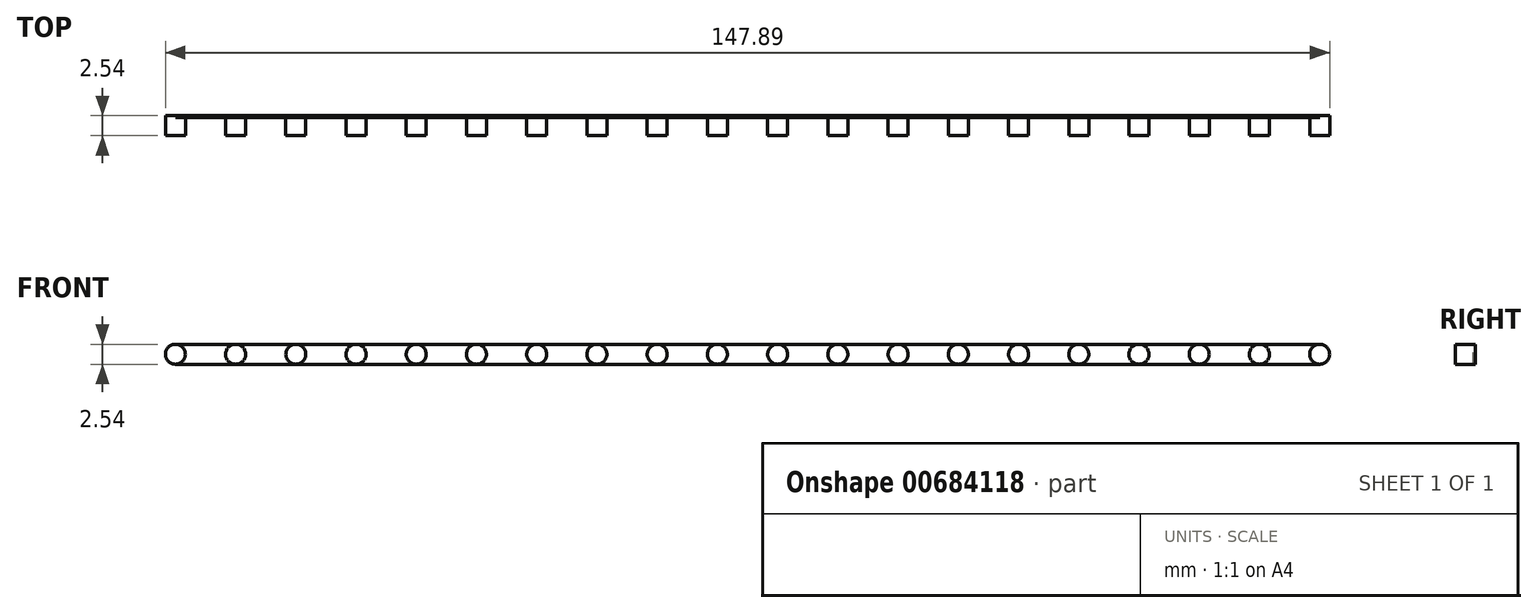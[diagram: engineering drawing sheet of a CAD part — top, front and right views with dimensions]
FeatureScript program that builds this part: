
annotation { "Feature Type Name" : "Feature", "Feature Type Description" : "" }
export const myFeature = defineFeature(function(context is Context, id is Id, definition is map)
    precondition{}
    {
        {
            var Q0;
            Q0=qCreatedBy(makeId("Front.planeOp"),FACE);
            var sketch = newSketch(context, id + "F0", { "sketchPlane" : qUnion([Q0])});
            skCircle(sketch, "E0", {"center": v(0, 0) * mm, "radius": 1.27 * mm});
            skCircle(sketch, "E1.1.0.0", {"center": v(7.65, 0) * mm, "radius": 1.27 * mm});
            skCircle(sketch, "E1.2.0.0", {"center": v(15.3, 0) * mm, "radius": 1.27 * mm});
            skLineSegment(sketch, "E1.direction1", {"start": v(0, 0) * mm, "end": v(7.65, 0) * mm, "construction": true});
            skCircle(sketch, "E2.0.3.0", {"center": v(22.95, 0) * mm, "radius": 1.27 * mm});
            skCircle(sketch, "E2.0.4.0", {"center": v(30.6, 0) * mm, "radius": 1.27 * mm});
            skCircle(sketch, "E2.0.5.0", {"center": v(38.25, 0) * mm, "radius": 1.27 * mm});
            skCircle(sketch, "E2.0.6.0", {"center": v(45.9, 0) * mm, "radius": 1.27 * mm});
            skCircle(sketch, "E2.0.7.0", {"center": v(53.55, 0) * mm, "radius": 1.27 * mm});
            skCircle(sketch, "E2.0.8.0", {"center": v(61.2, 0) * mm, "radius": 1.27 * mm});
            skCircle(sketch, "E2.0.9.0", {"center": v(68.85, 0) * mm, "radius": 1.27 * mm});
            skCircle(sketch, "E2.0.10.0", {"center": v(76.5, 0) * mm, "radius": 1.27 * mm});
            skCircle(sketch, "E2.0.11.0", {"center": v(84.15, 0) * mm, "radius": 1.27 * mm});
            skCircle(sketch, "E2.0.12.0", {"center": v(91.8, 0) * mm, "radius": 1.27 * mm});
            skCircle(sketch, "E2.0.13.0", {"center": v(99.45, 0) * mm, "radius": 1.27 * mm});
            skCircle(sketch, "E2.0.14.0", {"center": v(107.1, 0) * mm, "radius": 1.27 * mm});
            skCircle(sketch, "E2.0.15.0", {"center": v(114.75, 0) * mm, "radius": 1.27 * mm});
            skCircle(sketch, "E2.0.16.0", {"center": v(122.4, 0) * mm, "radius": 1.27 * mm});
            skCircle(sketch, "E2.0.17.0", {"center": v(130.05, 0) * mm, "radius": 1.27 * mm});
            skCircle(sketch, "E2.0.18.0", {"center": v(137.7, 0) * mm, "radius": 1.27 * mm});
            skCircle(sketch, "E2.0.19.0", {"center": v(145.35, 0) * mm, "radius": 1.27 * mm});
            skSolve(sketch);
        }
        {
            var Q0;
            Q0 = qSketchRegion(id + "F0", true);
            extrude(context, id + "F1", {"entities" : qUnion([Q0]), "depth" : 2.54 * mm, "offsetDistance" : 25.4 * mm});
        }
        {
            var Q0;
            Q0=qCreatedBy(makeId("Front.planeOp"),FACE);
            var sketch = newSketch(context, id + "F2", { "sketchPlane" : qUnion([Q0])});
            skLineSegment(sketch, "E3.bottom", {"start": v(145.35, -1.27) * mm, "end": v(0, -1.27) * mm});
            skLineSegment(sketch, "E3.top", {"start": v(145.35, 1.27) * mm, "end": v(0, 1.27) * mm});
            skLineSegment(sketch, "E3.left", {"start": v(145.35, -1.27) * mm, "end": v(145.35, 1.27) * mm});
            skLineSegment(sketch, "E3.right", {"start": v(0, -1.27) * mm, "end": v(0, 1.27) * mm});
            skLineSegment(sketch, "E4", {"start": v(146.62, 0) * mm, "end": v(144.08, 0) * mm});
            skPoint(sketch, "E5", {"position": v(145.35, 0) * mm});
            skSolve(sketch);
        }
        {
            var Q0;
            {var subQ0=sQuery(id+"F2.wireOp",EDGE,"E3.bottom");Q0=makeQuery(id+"F2.imprint","IMPRINT",FACE,{"disambiguationData":[TD([[makeQuery(id+"F2.imprint","IMPRINT",EDGE,{"derivedFrom":subQ0}),-1.0]])]});}
            extrude(context, id + "F3", {"entities" : qUnion([Q0]), "operationType" : NewBodyOperationType.ADD, "depth" : 0.25 * mm, "offsetDistance" : 25.4 * mm});
        }
    });
